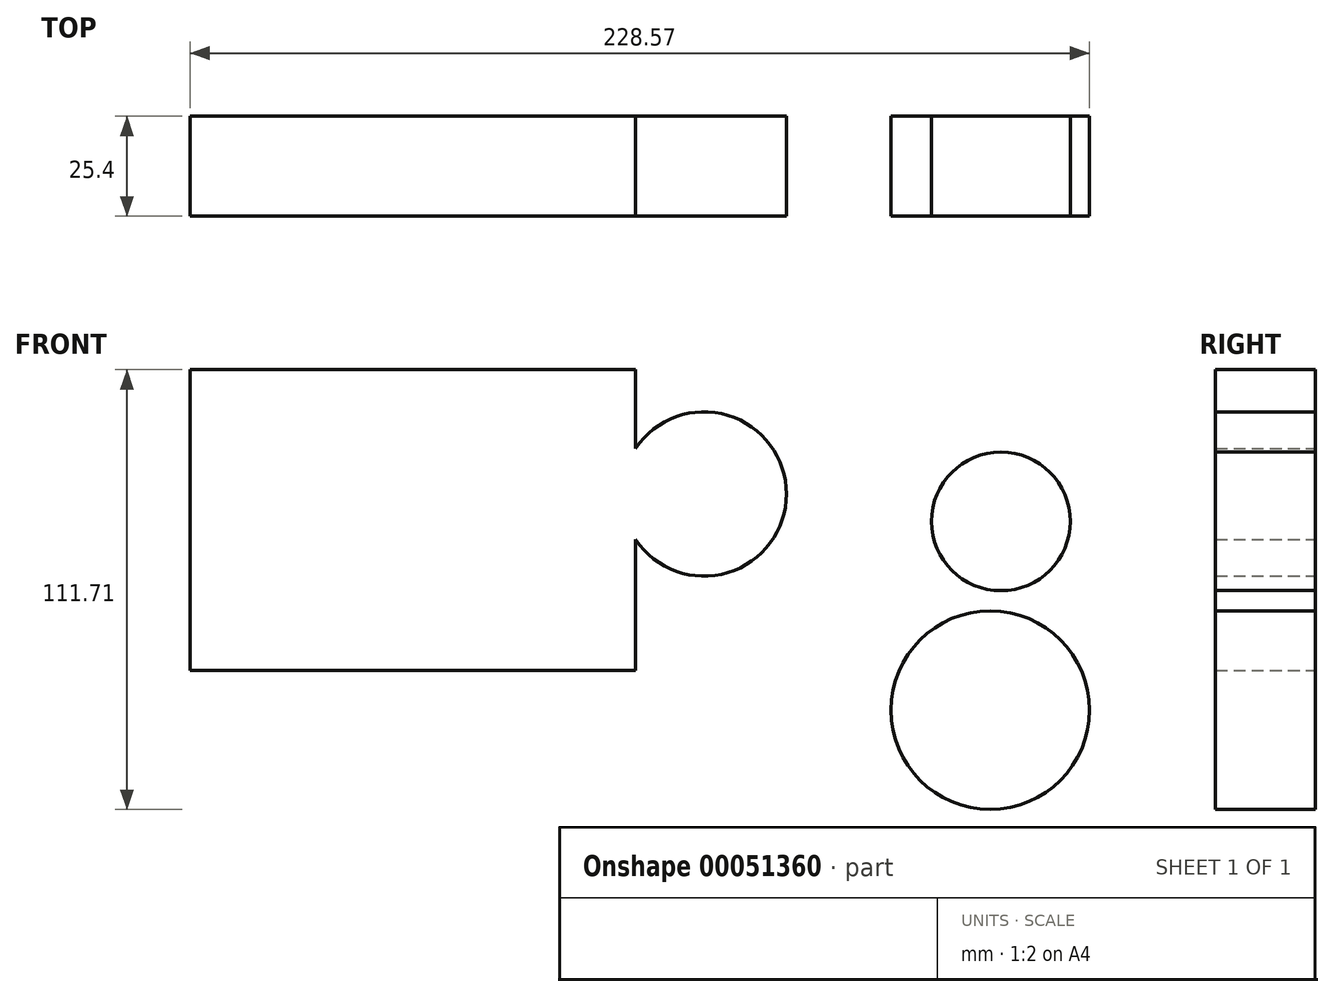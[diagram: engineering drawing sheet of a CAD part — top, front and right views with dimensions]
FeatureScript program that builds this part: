
annotation { "Feature Type Name" : "Feature", "Feature Type Description" : "" }
export const myFeature = defineFeature(function(context is Context, id is Id, definition is map)
    precondition{}
    {
        {
            var Q0;
            Q0=qCreatedBy(makeId("Front.planeOp"),FACE);
            var sketch = newSketch(context, id + "F0", { "sketchPlane" : qUnion([Q0])});
            skLineSegment(sketch, "E0.bottom", {"start": v(-103.86, 82.6) * mm, "end": v(9.4, 82.6) * mm});
            skLineSegment(sketch, "E0.top", {"start": v(-103.86, 6.2) * mm, "end": v(9.4, 6.2) * mm});
            skLineSegment(sketch, "E0.left", {"start": v(-103.86, 82.6) * mm, "end": v(-103.86, 6.2) * mm});
            skLineSegment(sketch, "E0.right", {"start": v(9.4, 82.6) * mm, "end": v(9.4, 6.2) * mm});
            skSolve(sketch);
        }
        {
            var Q0;
            Q0=makeQuery(id+"F0.imprint","IMPRINT",FACE,{"disambiguationData":[TD([[makeQuery(id+"F0.imprint","IMPRINT",EDGE,{"derivedFrom":sQuery(id+"F0.wireOp",EDGE,"E0.bottom")}),-1.0]])]});
            extrude(context, id + "F1", {"entities" : qUnion([Q0]), "depth" : 25.4 * mm});
        }
        {
            var Q0;
            Q0=qCreatedBy(makeId("Front.planeOp"),FACE);
            var sketch = newSketch(context, id + "F2", { "sketchPlane" : qUnion([Q0])});
            skCircle(sketch, "E1", {"center": v(26.78, 51) * mm, "radius": 20.88 * mm});
            skCircle(sketch, "E2", {"center": v(102.18, 44.05) * mm, "radius": 17.62 * mm});
            skCircle(sketch, "E3", {"center": v(99.49, -3.9) * mm, "radius": 25.22 * mm});
            skSolve(sketch);
        }
        {
            var Q0;
            Q0 = qSketchRegion(id + "F2", true);
            extrude(context, id + "F3", {"entities" : qUnion([Q0]), "operationType" : NewBodyOperationType.ADD, "depth" : 25.4 * mm});
        }
    });
